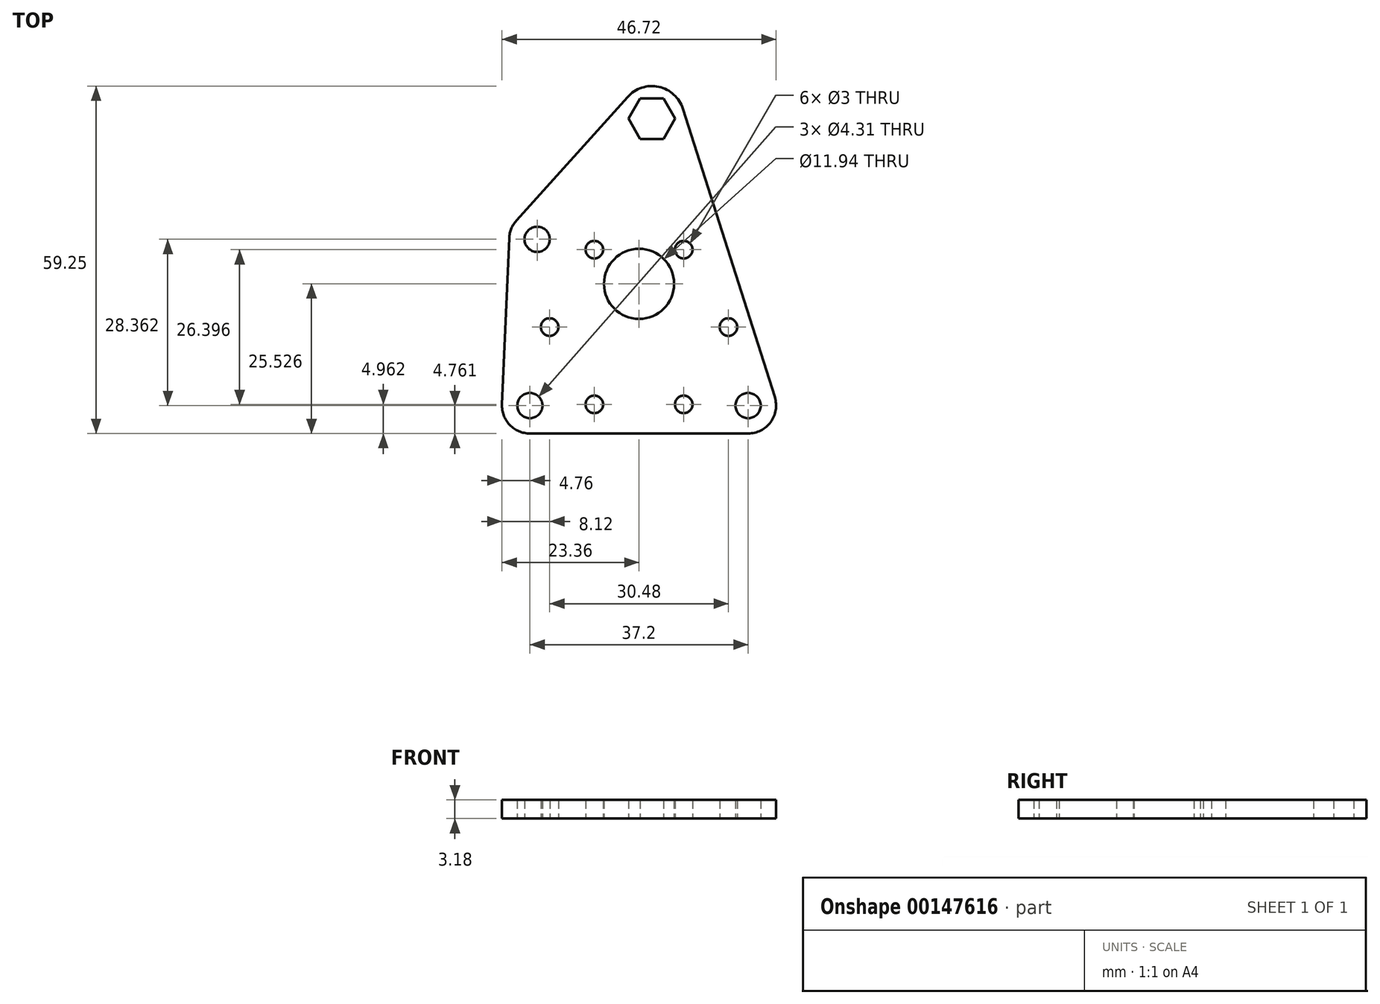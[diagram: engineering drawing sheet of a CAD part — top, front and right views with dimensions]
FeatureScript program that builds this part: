
annotation { "Feature Type Name" : "Feature", "Feature Type Description" : "" }
export const myFeature = defineFeature(function(context is Context, id is Id, definition is map)
    precondition{}
    {
        {
            var Q0;
            Q0=qCreatedBy(makeId("Top.planeOp"),FACE);
            var sketch = newSketch(context, id + "F0", { "sketchPlane" : qUnion([Q0])});
            skPoint(sketch, "E0.rect.middle", {"position": v(0, 0) * mm});
            skLineSegment(sketch, "E1", {"start": v(0, -7.37) * mm, "end": v(0, 7.37) * mm, "construction": true});
            skCircle(sketch, "E2.cCircle", {"center": v(0, 0) * mm, "radius": 13.2 * mm, "construction": true});
            skLineSegment(sketch, "E2.0", {"start": v(7.62, 13.2) * mm, "end": v(15.24, 0) * mm, "construction": true});
            skLineSegment(sketch, "E2.1", {"start": v(15.24, 0) * mm, "end": v(7.62, -13.2) * mm, "construction": true});
            skLineSegment(sketch, "E2.2", {"start": v(7.62, -13.2) * mm, "end": v(-7.62, -13.2) * mm, "construction": true});
            skLineSegment(sketch, "E2.3", {"start": v(-7.62, -13.2) * mm, "end": v(-15.24, 0) * mm, "construction": true});
            skLineSegment(sketch, "E2.4", {"start": v(-15.24, 0) * mm, "end": v(-7.62, 13.2) * mm, "construction": true});
            skLineSegment(sketch, "E2.5", {"start": v(-7.62, 13.2) * mm, "end": v(7.62, 13.2) * mm, "construction": true});
            skCircle(sketch, "E3", {"center": v(0, 0) * mm, "radius": 18.16 * mm, "construction": true});
            skCircle(sketch, "E4", {"center": v(7.62, 13.2) * mm, "radius": 2.92 * mm, "construction": true});
            skCircle(sketch, "E5", {"center": v(-7.62, 13.2) * mm, "radius": 1.5 * mm});
            skCircle(sketch, "E6", {"center": v(7.62, 13.2) * mm, "radius": 1.5 * mm});
            skCircle(sketch, "E7", {"center": v(15.24, 0) * mm, "radius": 1.5 * mm});
            skCircle(sketch, "E8", {"center": v(7.62, -13.2) * mm, "radius": 1.5 * mm});
            skCircle(sketch, "E9", {"center": v(-7.62, -13.2) * mm, "radius": 1.5 * mm});
            skCircle(sketch, "E10", {"center": v(-15.24, 0) * mm, "radius": 1.5 * mm});
            skCircle(sketch, "E11", {"center": v(0, 7.37) * mm, "radius": 5.97 * mm});
            skLineSegment(sketch, "E12.bottom", {"start": v(-18.6, -13.4) * mm, "end": v(18.6, -13.4) * mm, "construction": true});
            skCircle(sketch, "E13", {"center": v(-18.6, -13.4) * mm, "radius": 2.15 * mm});
            skCircle(sketch, "E14", {"center": v(18.6, -13.4) * mm, "radius": 2.15 * mm});
            skLineSegment(sketch, "E15", {"start": v(23.14, -11.95) * mm, "end": v(7.49, 37.22) * mm});
            skLineSegment(sketch, "E16", {"start": v(0, -7.37) * mm, "end": v(0, -13.4) * mm, "construction": true});
            skLineSegment(sketch, "E17", {"start": v(0, -13.4) * mm, "end": v(0, -18.16) * mm, "construction": true});
            skLineSegment(sketch, "E18", {"start": v(-18.6, -13.4) * mm, "end": v(-18.6, 14.96) * mm, "construction": true});
            skLineSegment(sketch, "E19", {"start": v(-18.6, 14.96) * mm, "end": v(-17.37, 14.96) * mm, "construction": true});
            skArc(sketch, "E20", {"start": v(-20.9, 18.15) * mm, "mid": v(-21.78, 16.76) * mm, "end": v(-22.12, 15.17) * mm});
            skArc(sketch, "E21", {"start": v(-23.36, -13.2) * mm, "mid": v(-22.04, -16.7) * mm, "end": v(-18.6, -18.16) * mm});
            skLineSegment(sketch, "E22", {"start": v(-22.12, 15.17) * mm, "end": v(-23.36, -13.2) * mm});
            skLineSegment(sketch, "E23", {"start": v(-18.6, -18.16) * mm, "end": v(18.6, -18.16) * mm});
            skLineSegment(sketch, "E24", {"start": v(-20.9, 18.15) * mm, "end": v(-1.94, 39.25) * mm});
            skArc(sketch, "E25", {"start": v(7.49, 37.22) * mm, "mid": v(3.36, 40.97) * mm, "end": v(-1.94, 39.25) * mm});
            skLineSegment(sketch, "E26", {"start": v(-17.37, 14.96) * mm, "end": v(-17.37, 35.54) * mm, "construction": true});
            skLineSegment(sketch, "E27", {"start": v(-17.37, 35.54) * mm, "end": v(2.2, 35.54) * mm, "construction": true});
            skArc(sketch, "E28", {"start": v(18.6, -18.16) * mm, "mid": v(22.44, -16.2) * mm, "end": v(23.14, -11.95) * mm});
            skCircle(sketch, "E29.cCircle", {"center": v(2.2, 35.54) * mm, "radius": 3.97 * mm, "construction": true});
            skLineSegment(sketch, "E29.0", {"start": v(4.18, 32.1) * mm, "end": v(0.2, 32.1) * mm});
            skLineSegment(sketch, "E29.1", {"start": v(0.2, 32.1) * mm, "end": v(-1.78, 35.54) * mm});
            skLineSegment(sketch, "E29.2", {"start": v(-1.78, 35.54) * mm, "end": v(0.2, 38.98) * mm});
            skLineSegment(sketch, "E29.3", {"start": v(0.2, 38.98) * mm, "end": v(4.18, 38.98) * mm});
            skLineSegment(sketch, "E29.4", {"start": v(4.18, 38.98) * mm, "end": v(6.16, 35.54) * mm});
            skLineSegment(sketch, "E29.5", {"start": v(6.16, 35.54) * mm, "end": v(4.18, 32.1) * mm});
            skCircle(sketch, "E30", {"center": v(-17.37, 14.96) * mm, "radius": 2.15 * mm});
            skSolve(sketch);
        }
        {
            var Q0;
            Q0=qSketchRegion(id+"F0",true);
            extrude(context, id + "F1", {"entities" : qUnion([Q0]), "depth" : 3.17 * mm});
        }
    });
